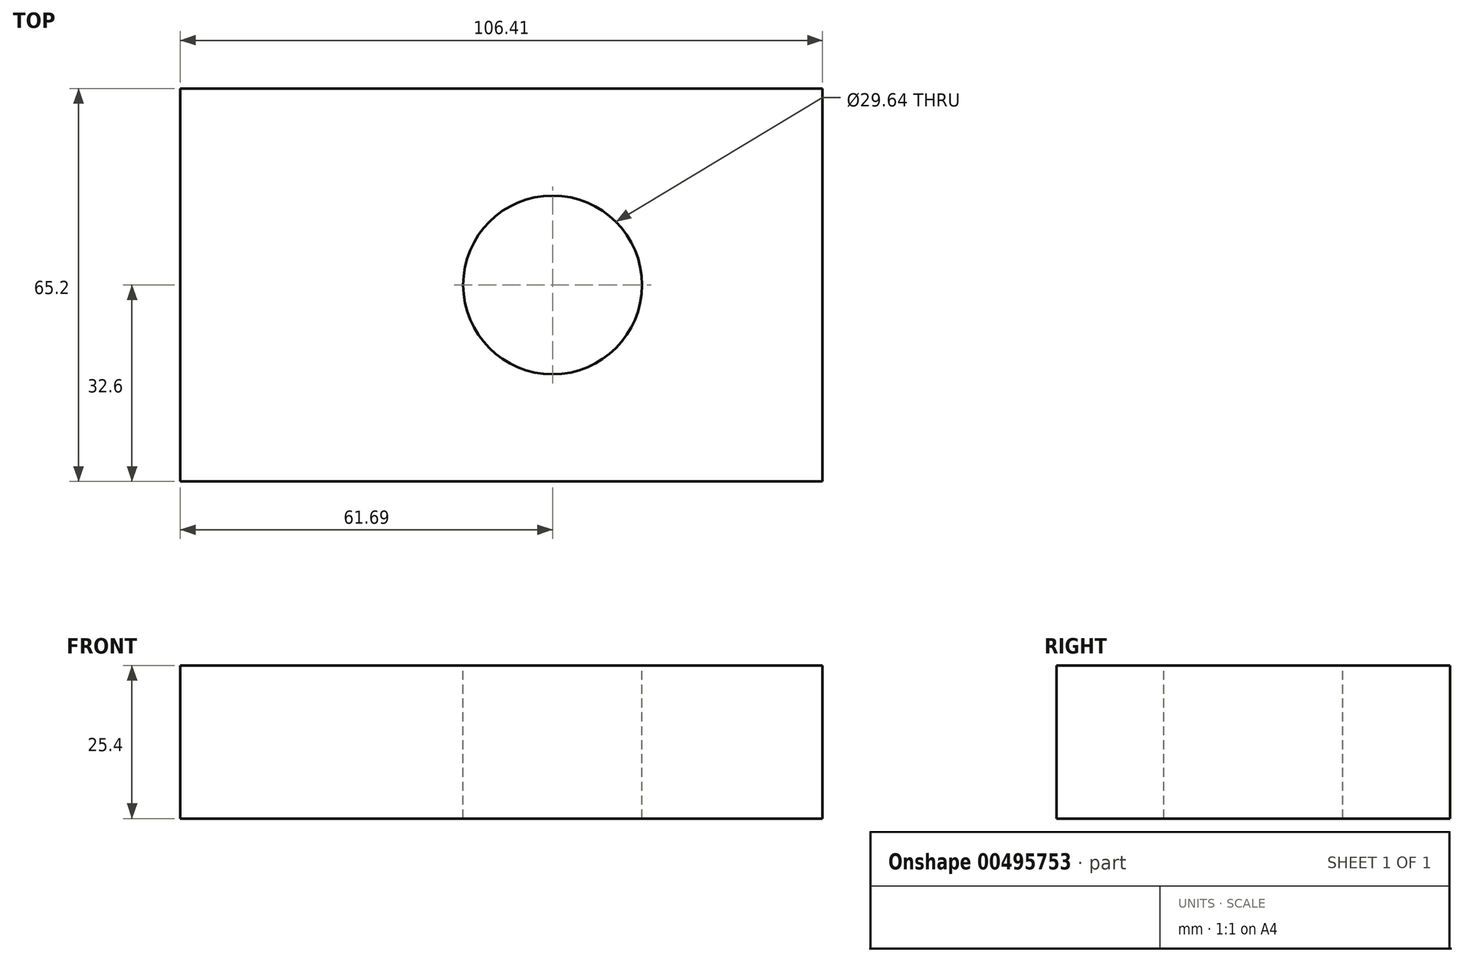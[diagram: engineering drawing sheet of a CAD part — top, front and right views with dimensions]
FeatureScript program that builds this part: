
annotation { "Feature Type Name" : "Feature", "Feature Type Description" : "" }
export const myFeature = defineFeature(function(context is Context, id is Id, definition is map)
    precondition{}
    {
        {
            var Q0;
            Q0=qCreatedBy(makeId("Top.planeOp"),FACE);
            var sketch = newSketch(context, id + "F0", { "sketchPlane" : qUnion([Q0])});
            skLineSegment(sketch, "E0", {"start": v(-61.7, 32.6) * mm, "end": v(-61.7, -32.6) * mm});
            skLineSegment(sketch, "E1", {"start": v(-61.7, -32.6) * mm, "end": v(44.72, -32.6) * mm});
            skLineSegment(sketch, "E2", {"start": v(44.72, -32.6) * mm, "end": v(44.72, 32.6) * mm});
            skLineSegment(sketch, "E3", {"start": v(44.72, 32.6) * mm, "end": v(-61.7, 32.6) * mm});
            skSolve(sketch);
        }
        {
            var Q0;
            Q0=makeQuery(id+"F0.imprint","IMPRINT",FACE,{"disambiguationData":[TD([[makeQuery(id+"F0.imprint","IMPRINT",EDGE,{"derivedFrom":sQuery(id+"F0.wireOp",EDGE,"E0")}),1.0]])]});
            extrude(context, id + "F1", {"entities" : qUnion([Q0]), "depth" : 25.4 * mm});
        }
        {
            var Q0;
            Q0=makeQuery(id+"F1.opExtrude","CAP_FACE",FACE,{"disambiguationData":[OSD([sQuery(id+"F0.wireOp",EDGE,"E0"),sQuery(id+"F0.wireOp",EDGE,"E1"),sQuery(id+"F0.wireOp",EDGE,"E2"),sQuery(id+"F0.wireOp",EDGE,"E3")])],"isStart":false});
            var sketch = newSketch(context, id + "F2", { "sketchPlane" : qUnion([Q0])});
            skCircle(sketch, "E4", {"center": v(0, 0) * mm, "radius": 14.82 * mm});
            skSolve(sketch);
        }
        {
            var Q0;
            Q0=makeQuery(id+"F2.imprint","IMPRINT",FACE,{"disambiguationData":[TD([[makeQuery(id+"F2.imprint","IMPRINT",EDGE,{"derivedFrom":sQuery(id+"F2.wireOp",EDGE,"E4")}),1.0]])]});
            extrude(context, id + "F3", {"entities" : qUnion([Q0]), "operationType" : NewBodyOperationType.REMOVE, "oppositeDirection" : true, "depth" : 125.48 * mm});
        }
    });
